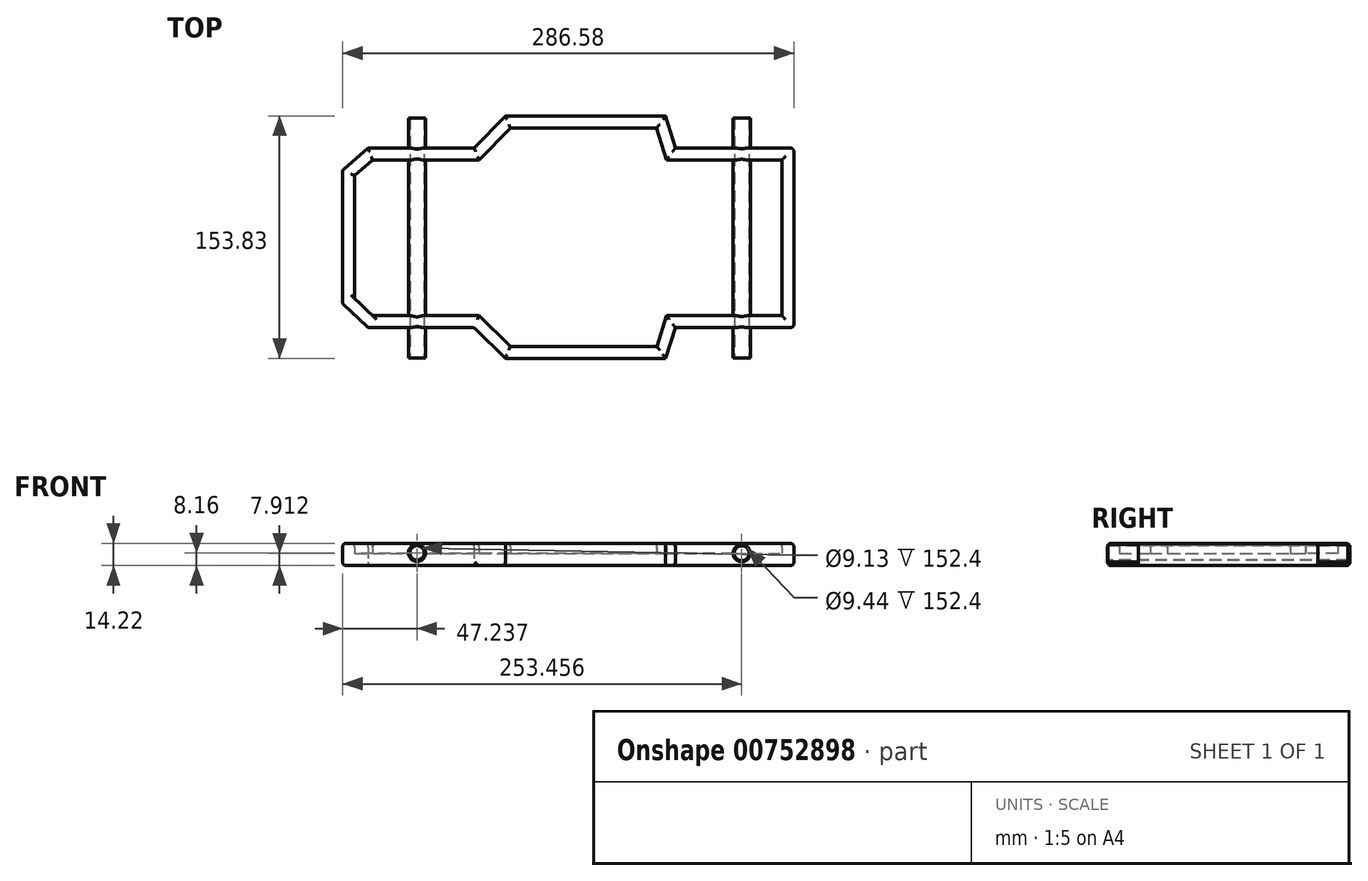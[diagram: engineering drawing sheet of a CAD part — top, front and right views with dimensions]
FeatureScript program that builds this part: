
annotation { "Feature Type Name" : "Feature", "Feature Type Description" : "" }
export const myFeature = defineFeature(function(context is Context, id is Id, definition is map)
    precondition{}
    {
        {
            var Q0;
            Q0=qCreatedBy(makeId("Top.planeOp"),FACE);
            var sketch = newSketch(context, id + "F0", { "sketchPlane" : qUnion([Q0])});
            skLineSegment(sketch, "E0", {"start": v(-146.4, -41.77) * mm, "end": v(-146.4, 43) * mm});
            skLineSegment(sketch, "E1", {"start": v(-146.4, 43) * mm, "end": v(-130.26, 57.07) * mm});
            skLineSegment(sketch, "E2", {"start": v(-130.26, 57.07) * mm, "end": v(-62.86, 57.07) * mm});
            skLineSegment(sketch, "E3", {"start": v(-62.86, 57.07) * mm, "end": v(-43, 77.33) * mm});
            skLineSegment(sketch, "E4", {"start": v(-43, 77.33) * mm, "end": v(58.72, 77.33) * mm});
            skLineSegment(sketch, "E5", {"start": v(58.72, 77.33) * mm, "end": v(64.93, 57.07) * mm});
            skLineSegment(sketch, "E6", {"start": v(64.93, 57.07) * mm, "end": v(140.19, 57.07) * mm});
            skLineSegment(sketch, "E7", {"start": v(140.19, 57.07) * mm, "end": v(140.19, -57.07) * mm});
            skLineSegment(sketch, "E8", {"start": v(140.19, -57.07) * mm, "end": v(64.93, -57.07) * mm});
            skLineSegment(sketch, "E9", {"start": v(64.93, -57.07) * mm, "end": v(58.72, -76.5) * mm});
            skLineSegment(sketch, "E10", {"start": v(58.72, -76.5) * mm, "end": v(-43, -76.5) * mm});
            skLineSegment(sketch, "E11", {"start": v(-43, -76.5) * mm, "end": v(-62.86, -57.07) * mm});
            skLineSegment(sketch, "E12", {"start": v(-62.86, -57.07) * mm, "end": v(-130.26, -57.07) * mm});
            skLineSegment(sketch, "E13", {"start": v(-130.26, -57.07) * mm, "end": v(-146.4, -41.77) * mm});
            skSolve(sketch);
        }
        {
            var Q0;
            Q0 = qSketchRegion(id + "F0", true);
            extrude(context, id + "F1", {"entities" : qUnion([Q0]), "depth" : 14.22 * mm, "offsetDistance" : 25.4 * mm});
        }
        {
            var Q0;
            Q0=makeQuery(id+"F1.opExtrude","CAP_FACE",FACE,{"disambiguationData":[OSD([sQuery(id+"F0.wireOp",EDGE,"E0"),sQuery(id+"F0.wireOp",EDGE,"E1"),sQuery(id+"F0.wireOp",EDGE,"E2"),sQuery(id+"F0.wireOp",EDGE,"E3"),sQuery(id+"F0.wireOp",EDGE,"E4"),sQuery(id+"F0.wireOp",EDGE,"E5"),sQuery(id+"F0.wireOp",EDGE,"E6"),sQuery(id+"F0.wireOp",EDGE,"E7"),sQuery(id+"F0.wireOp",EDGE,"E8"),sQuery(id+"F0.wireOp",EDGE,"E9"),sQuery(id+"F0.wireOp",EDGE,"E10"),sQuery(id+"F0.wireOp",EDGE,"E11"),sQuery(id+"F0.wireOp",EDGE,"E12"),sQuery(id+"F0.wireOp",EDGE,"E13")])],"isStart":false});
            shell(context, id + "F2", {"entities" : qUnion([Q0]), "thickness" : 7.62 * mm});
        }
        {
            var Q0;
            {var subQ0=sQuery(id+"F0.wireOp",EDGE,"E2");Q0=makeQuery(id+"F2.opShell","OFFSET_EDGE",EDGE,{"disambiguationData":[OSD([subQ0]),TDD([makeQuery(id+"F1.opExtrude","CAP_EDGE",EDGE,{"disambiguationData":[OSD([subQ0])],"isStart":false})])]});}
            var Q1;
            {var subQ0=sQuery(id+"F0.wireOp",EDGE,"E3");Q1=makeQuery(id+"F2.opShell","OFFSET_EDGE",EDGE,{"disambiguationData":[OSD([subQ0]),TDD([makeQuery(id+"F1.opExtrude","CAP_EDGE",EDGE,{"disambiguationData":[OSD([subQ0])],"isStart":false})])]});}
            var Q2;
            {var subQ0=sQuery(id+"F0.wireOp",EDGE,"E1");Q2=makeQuery(id+"F2.opShell","OFFSET_EDGE",EDGE,{"disambiguationData":[OSD([subQ0]),TDD([makeQuery(id+"F1.opExtrude","CAP_EDGE",EDGE,{"disambiguationData":[OSD([subQ0])],"isStart":false})])]});}
            var Q3;
            {var subQ0=sQuery(id+"F0.wireOp",EDGE,"E0");Q3=makeQuery(id+"F2.opShell","OFFSET_EDGE",EDGE,{"disambiguationData":[OSD([subQ0]),TDD([makeQuery(id+"F1.opExtrude","CAP_EDGE",EDGE,{"disambiguationData":[OSD([subQ0])],"isStart":false})])]});}
            var Q4;
            Q4=makeQuery(id+"F1.opExtrude","CAP_EDGE",EDGE,{"disambiguationData":[OSD([sQuery(id+"F0.wireOp",EDGE,"E2")])],"isStart":false});
            var Q5;
            Q5=makeQuery(id+"F1.opExtrude","CAP_EDGE",EDGE,{"disambiguationData":[OSD([sQuery(id+"F0.wireOp",EDGE,"E3")])],"isStart":false});
            var Q6;
            Q6=makeQuery(id+"F1.opExtrude","CAP_EDGE",EDGE,{"disambiguationData":[OSD([sQuery(id+"F0.wireOp",EDGE,"E4")])],"isStart":false});
            var Q7;
            {var subQ0=sQuery(id+"F0.wireOp",EDGE,"E4");Q7=makeQuery(id+"F2.opShell","OFFSET_EDGE",EDGE,{"disambiguationData":[OSD([subQ0]),TDD([makeQuery(id+"F1.opExtrude","CAP_EDGE",EDGE,{"disambiguationData":[OSD([subQ0])],"isStart":false})])]});}
            var Q8;
            {var subQ0=sQuery(id+"F0.wireOp",EDGE,"E5");Q8=makeQuery(id+"F2.opShell","OFFSET_EDGE",EDGE,{"disambiguationData":[OSD([subQ0]),TDD([makeQuery(id+"F1.opExtrude","CAP_EDGE",EDGE,{"disambiguationData":[OSD([subQ0])],"isStart":false})])]});}
            var Q9;
            Q9=makeQuery(id+"F1.opExtrude","CAP_EDGE",EDGE,{"disambiguationData":[OSD([sQuery(id+"F0.wireOp",EDGE,"E5")])],"isStart":false});
            var Q10;
            Q10=makeQuery(id+"F1.opExtrude","CAP_EDGE",EDGE,{"disambiguationData":[OSD([sQuery(id+"F0.wireOp",EDGE,"E6")])],"isStart":false});
            var Q11;
            {var subQ0=sQuery(id+"F0.wireOp",EDGE,"E6");Q11=makeQuery(id+"F2.opShell","OFFSET_EDGE",EDGE,{"disambiguationData":[OSD([subQ0]),TDD([makeQuery(id+"F1.opExtrude","CAP_EDGE",EDGE,{"disambiguationData":[OSD([subQ0])],"isStart":false})])]});}
            var Q12;
            {var subQ0=sQuery(id+"F0.wireOp",EDGE,"E7");Q12=makeQuery(id+"F2.opShell","OFFSET_EDGE",EDGE,{"disambiguationData":[OSD([subQ0]),TDD([makeQuery(id+"F1.opExtrude","CAP_EDGE",EDGE,{"disambiguationData":[OSD([subQ0])],"isStart":false})])]});}
            var Q13;
            Q13=makeQuery(id+"F1.opExtrude","CAP_EDGE",EDGE,{"disambiguationData":[OSD([sQuery(id+"F0.wireOp",EDGE,"E7")])],"isStart":false});
            var Q14;
            Q14=makeQuery(id+"F1.opExtrude","CAP_EDGE",EDGE,{"disambiguationData":[OSD([sQuery(id+"F0.wireOp",EDGE,"E8")])],"isStart":false});
            var Q15;
            {var subQ0=sQuery(id+"F0.wireOp",EDGE,"E8");Q15=makeQuery(id+"F2.opShell","OFFSET_EDGE",EDGE,{"disambiguationData":[OSD([subQ0]),TDD([makeQuery(id+"F1.opExtrude","CAP_EDGE",EDGE,{"disambiguationData":[OSD([subQ0])],"isStart":false})])]});}
            var Q16;
            {var subQ0=sQuery(id+"F0.wireOp",EDGE,"E9");Q16=makeQuery(id+"F2.opShell","OFFSET_EDGE",EDGE,{"disambiguationData":[OSD([subQ0]),TDD([makeQuery(id+"F1.opExtrude","CAP_EDGE",EDGE,{"disambiguationData":[OSD([subQ0])],"isStart":false})])]});}
            var Q17;
            Q17=makeQuery(id+"F1.opExtrude","CAP_EDGE",EDGE,{"disambiguationData":[OSD([sQuery(id+"F0.wireOp",EDGE,"E9")])],"isStart":false});
            var Q18;
            {var subQ0=sQuery(id+"F0.wireOp",EDGE,"E10");Q18=makeQuery(id+"F2.opShell","OFFSET_EDGE",EDGE,{"disambiguationData":[OSD([subQ0]),TDD([makeQuery(id+"F1.opExtrude","CAP_EDGE",EDGE,{"disambiguationData":[OSD([subQ0])],"isStart":false})])]});}
            var Q19;
            Q19=makeQuery(id+"F1.opExtrude","CAP_EDGE",EDGE,{"disambiguationData":[OSD([sQuery(id+"F0.wireOp",EDGE,"E10")])],"isStart":false});
            var Q20;
            Q20=makeQuery(id+"F1.opExtrude","CAP_EDGE",EDGE,{"disambiguationData":[OSD([sQuery(id+"F0.wireOp",EDGE,"E11")])],"isStart":false});
            var Q21;
            {var subQ0=sQuery(id+"F0.wireOp",EDGE,"E11");Q21=makeQuery(id+"F2.opShell","OFFSET_EDGE",EDGE,{"disambiguationData":[OSD([subQ0]),TDD([makeQuery(id+"F1.opExtrude","CAP_EDGE",EDGE,{"disambiguationData":[OSD([subQ0])],"isStart":false})])]});}
            var Q22;
            {var subQ0=sQuery(id+"F0.wireOp",EDGE,"E12");Q22=makeQuery(id+"F2.opShell","OFFSET_EDGE",EDGE,{"disambiguationData":[OSD([subQ0]),TDD([makeQuery(id+"F1.opExtrude","CAP_EDGE",EDGE,{"disambiguationData":[OSD([subQ0])],"isStart":false})])]});}
            var Q23;
            Q23=makeQuery(id+"F1.opExtrude","CAP_EDGE",EDGE,{"disambiguationData":[OSD([sQuery(id+"F0.wireOp",EDGE,"E12")])],"isStart":false});
            var Q24;
            Q24=makeQuery(id+"F1.opExtrude","CAP_EDGE",EDGE,{"disambiguationData":[OSD([sQuery(id+"F0.wireOp",EDGE,"E13")])],"isStart":false});
            var Q25;
            Q25=makeQuery(id+"F1.opExtrude","CAP_EDGE",EDGE,{"disambiguationData":[OSD([sQuery(id+"F0.wireOp",EDGE,"E0")])],"isStart":false});
            var Q26;
            Q26=makeQuery(id+"F1.opExtrude","SWEPT_FACE",FACE,{"disambiguationData":[OSD([sQuery(id+"F0.wireOp",EDGE,"E0")])]});
            var Q27;
            Q27=makeQuery(id+"F1.opExtrude","CAP_EDGE",EDGE,{"disambiguationData":[OSD([sQuery(id+"F0.wireOp",EDGE,"E1")])],"isStart":false});
            var Q28;
            Q28=makeQuery(id+"F1.opExtrude","SWEPT_FACE",FACE,{"disambiguationData":[OSD([sQuery(id+"F0.wireOp",EDGE,"E12")])]});
            var Q29;
            Q29=makeQuery(id+"F1.opExtrude","SWEPT_FACE",FACE,{"disambiguationData":[OSD([sQuery(id+"F0.wireOp",EDGE,"E13")])]});
            var Q30;
            Q30=makeQuery(id+"F1.opExtrude","CAP_EDGE",EDGE,{"disambiguationData":[OSD([sQuery(id+"F0.wireOp",EDGE,"E10")])],"isStart":true});
            var Q31;
            Q31=makeQuery(id+"F1.opExtrude","CAP_EDGE",EDGE,{"disambiguationData":[OSD([sQuery(id+"F0.wireOp",EDGE,"E4")])],"isStart":true});
            var Q32;
            Q32=makeQuery(id+"F1.opExtrude","CAP_EDGE",EDGE,{"disambiguationData":[OSD([sQuery(id+"F0.wireOp",EDGE,"E2")])],"isStart":true});
            var Q33;
            Q33=makeQuery(id+"F1.opExtrude","CAP_EDGE",EDGE,{"disambiguationData":[OSD([sQuery(id+"F0.wireOp",EDGE,"E3")])],"isStart":true});
            var Q34;
            Q34=makeQuery(id+"F1.opExtrude","CAP_EDGE",EDGE,{"disambiguationData":[OSD([sQuery(id+"F0.wireOp",EDGE,"E6")])],"isStart":true});
            var Q35;
            Q35=makeQuery(id+"F1.opExtrude","CAP_EDGE",EDGE,{"disambiguationData":[OSD([sQuery(id+"F0.wireOp",EDGE,"E5")])],"isStart":true});
            var Q36;
            Q36=makeQuery(id+"F1.opExtrude","SWEPT_FACE",FACE,{"disambiguationData":[OSD([sQuery(id+"F0.wireOp",EDGE,"E7")])]});
            var Q37;
            Q37=makeQuery(id+"F1.opExtrude","CAP_EDGE",EDGE,{"disambiguationData":[OSD([sQuery(id+"F0.wireOp",EDGE,"E8")])],"isStart":true});
            var Q38;
            Q38=makeQuery(id+"F1.opExtrude","CAP_EDGE",EDGE,{"disambiguationData":[OSD([sQuery(id+"F0.wireOp",EDGE,"E9")])],"isStart":true});
            var Q39;
            Q39=makeQuery(id+"F1.opExtrude","CAP_EDGE",EDGE,{"disambiguationData":[OSD([sQuery(id+"F0.wireOp",EDGE,"E1")])],"isStart":true});
            fillet(context, id + "F3", {"entities" : qUnion([Q0, Q1, Q2, Q3, Q4, Q5, Q6, Q7, Q8, Q9, Q10, Q11, Q12, Q13, Q14, Q15, Q16, Q17, Q18, Q19, Q20, Q21, Q22, Q23, Q24, Q25, Q26, Q27, Q28, Q29, Q30, Q31, Q32, Q33, Q34, Q35, Q36, Q37, Q38, Q39]), "radius" : 2.3 * mm, "tangentPropagation" : true, "allowEdgeOverflow" : false});
        }
        {
            var Q0;
            Q0=qCreatedBy(makeId("Front.planeOp"),FACE);
            var sketch = newSketch(context, id + "F4", { "sketchPlane" : qUnion([Q0])});
            skCircle(sketch, "E14", {"center": v(-99.15, 8.16) * mm, "radius": 5.46 * mm});
            skSolve(sketch);
        }
        {
            var Q0;
            Q0 = qSketchRegion(id + "F4", true);
            extrude(context, id + "F5", {"entities" : qUnion([Q0]), "operationType" : NewBodyOperationType.ADD, "oppositeDirection" : true, "depth" : 76.2 * mm, "offsetDistance" : 25.4 * mm, "hasSecondDirection" : true, "secondDirectionOppositeDirection" : false, "secondDirectionDepth" : 76.2 * mm});
        }
        {
            var Q0;
            Q0=qCreatedBy(makeId("Front.planeOp"),FACE);
            var sketch = newSketch(context, id + "F6", { "sketchPlane" : qUnion([Q0])});
            skCircle(sketch, "E15", {"center": v(107.07, 7.91) * mm, "radius": 5.46 * mm});
            skSolve(sketch);
        }
        {
            var Q0;
            Q0 = qSketchRegion(id + "F6", true);
            extrude(context, id + "F7", {"entities" : qUnion([Q0]), "operationType" : NewBodyOperationType.ADD, "depth" : 76.2 * mm, "offsetDistance" : 25.4 * mm, "hasSecondDirection" : true, "secondDirectionOppositeDirection" : true, "secondDirectionDepth" : 76.2 * mm});
        }
        {
            var Q0;
            Q0=qCreatedBy(makeId("Front.planeOp"),FACE);
            var sketch = newSketch(context, id + "F8", { "sketchPlane" : qUnion([Q0])});
            skPoint(sketch, "E16.0", {"position": v(-99.15, 8.16) * mm});
            skCircle(sketch, "E17", {"center": v(-99.15, 8.16) * mm, "radius": 4.57 * mm});
            skSolve(sketch);
        }
        {
            var Q0;
            Q0 = qSketchRegion(id + "F8", true);
            extrude(context, id + "F9", {"entities" : qUnion([Q0]), "operationType" : NewBodyOperationType.REMOVE, "oppositeDirection" : true, "depth" : 92.96 * mm, "offsetDistance" : 25.4 * mm, "hasSecondDirection" : true, "secondDirectionOppositeDirection" : false, "secondDirectionDepth" : 84.84 * mm});
        }
        {
            var Q0;
            Q0=makeQuery(id+"F7.opExtrude","CAP_FACE",FACE,{"disambiguationData":[OSD([sQuery(id+"F6.wireOp",EDGE,"E15")])],"isStart":false});
            var sketch = newSketch(context, id + "F10", { "sketchPlane" : qUnion([Q0])});
            skCircle(sketch, "E18.0.0", {"center": v(107.07, 7.91) * mm, "radius": 5.46 * mm});
            skCircle(sketch, "E19", {"center": v(107.07, 7.91) * mm, "radius": 4.72 * mm});
            skSolve(sketch);
        }
        {
            var Q0;
            Q0=makeQuery(id+"F10.imprint","IMPRINT",FACE,{"disambiguationData":[TD([[makeQuery(id+"F10.imprint","IMPRINT",EDGE,{"derivedFrom":sQuery(id+"F10.wireOp",EDGE,"E19")}),1.0]])]});
            var Q1;
            Q1=sQuery(id+"F10.wireOp",EDGE,"E19");
            extrude(context, id + "F11", {"entities" : qUnion([Q0]), "operationType" : NewBodyOperationType.REMOVE, "surfaceEntities" : qUnion([Q1]), "endBound" : BoundingType.THROUGH_ALL, "oppositeDirection" : true, "depth" : 165.1 * mm, "offsetDistance" : 25.4 * mm});
        }
    });
